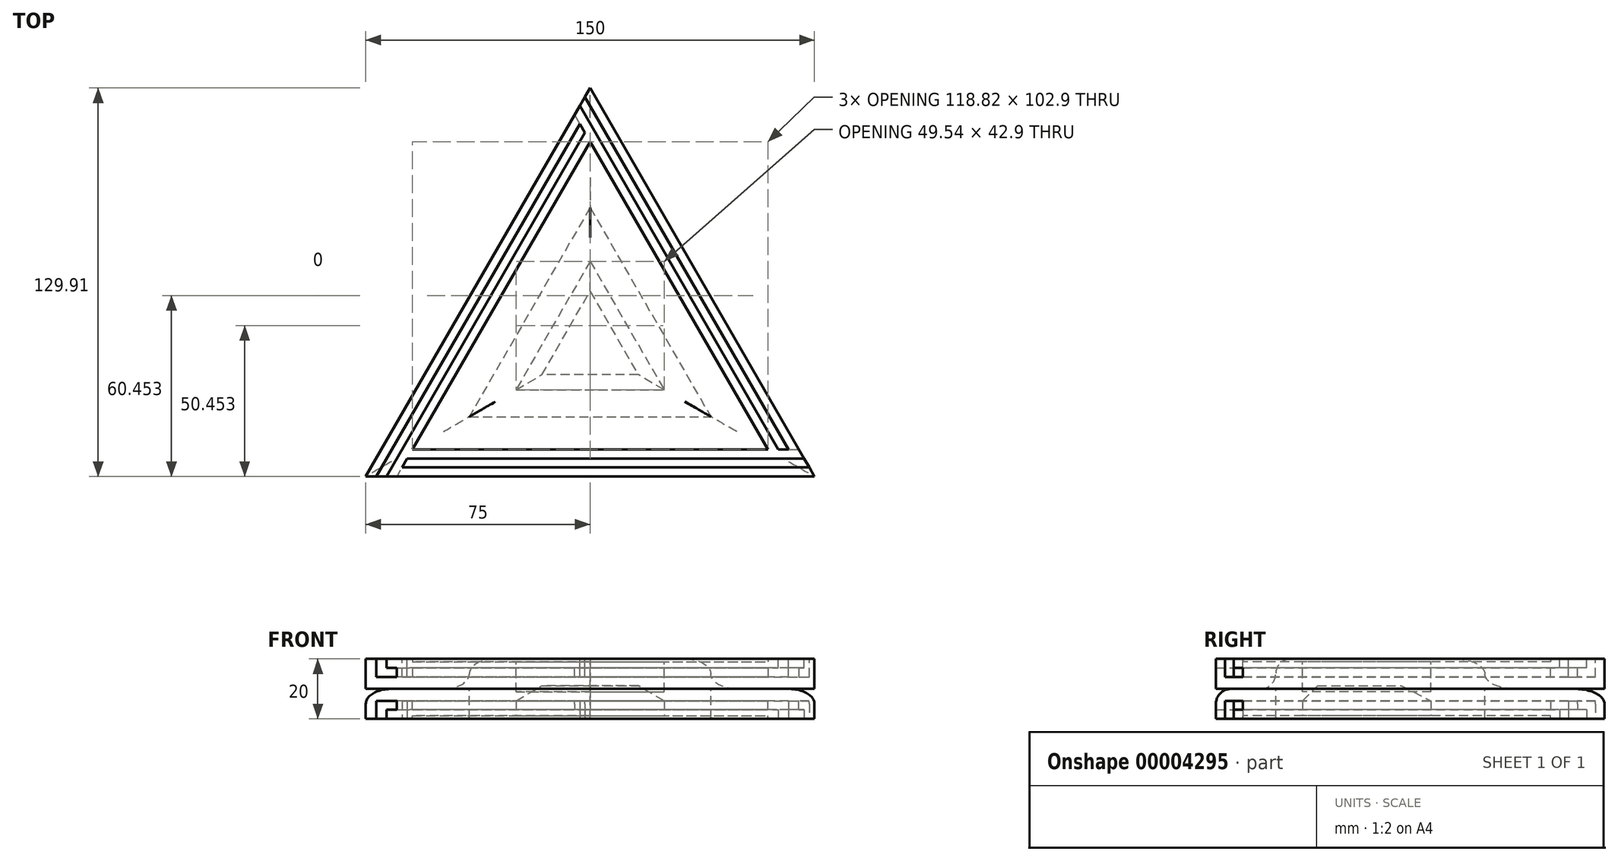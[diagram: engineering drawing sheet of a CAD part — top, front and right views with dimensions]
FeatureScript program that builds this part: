
annotation { "Feature Type Name" : "Feature", "Feature Type Description" : "" }
export const myFeature = defineFeature(function(context is Context, id is Id, definition is map)
    precondition{}
    {
        {
            var Q0;
            Q0=qCreatedBy(makeId("Top.planeOp"),FACE);
            var sketch = newSketch(context, id + "F0", { "sketchPlane" : qUnion([Q0])});
            skLineSegment(sketch, "E0.0", {"start": v(-75, -54.93) * mm, "end": v(75, -54.93) * mm});
            skLineSegment(sketch, "E1", {"start": v(0, 74.98) * mm, "end": v(-75, -54.93) * mm});
            skLineSegment(sketch, "E2", {"start": v(0, 74.98) * mm, "end": v(75, -54.93) * mm});
            skSolve(sketch);
        }
        {
            var Q0;
            Q0=makeQuery(id+"F0.imprint","IMPRINT",FACE,{"disambiguationData":[TD([[makeQuery(id+"F0.imprint","IMPRINT",EDGE,{"derivedFrom":sQuery(id+"F0.wireOp",EDGE,"E0.0")}),1.0]])]});
            extrude(context, id + "F1", {"entities" : qUnion([Q0]), "depth" : 10 * mm});
        }
        {
            var Q0;
            Q0=makeQuery(id+"F1.opExtrude","CAP_FACE",FACE,{"disambiguationData":[OSD([sQuery(id+"F0.wireOp",EDGE,"E0.0"),sQuery(id+"F0.wireOp",EDGE,"E1"),sQuery(id+"F0.wireOp",EDGE,"E2")])],"isStart":true});
            var sketch = newSketch(context, id + "F2", { "sketchPlane" : qUnion([Q0])});
            skLineSegment(sketch, "E3.0", {"start": v(-40.36, 34.93) * mm, "end": v(40.36, 34.93) * mm});
            skLineSegment(sketch, "E3.1", {"start": v(0, -34.98) * mm, "end": v(-40.36, 34.93) * mm});
            skLineSegment(sketch, "E3.2", {"start": v(0, -34.98) * mm, "end": v(40.36, 34.93) * mm});
            skSolve(sketch);
        }
        {
            var Q0;
            Q0=makeQuery(id+"F2.imprint","IMPRINT",FACE,{"disambiguationData":[TD([[makeQuery(id+"F2.imprint","IMPRINT",EDGE,{"derivedFrom":sQuery(id+"F2.wireOp",EDGE,"E3.0")}),-1.0]])]});
            extrude(context, id + "F3", {"entities" : qUnion([Q0]), "operationType" : NewBodyOperationType.ADD, "depth" : 10 * mm});
        }
        {
            var Q0;
            Q0=makeQuery(id+"F1.opExtrude","CAP_FACE",FACE,{"disambiguationData":[OSD([sQuery(id+"F0.wireOp",EDGE,"E0.0"),sQuery(id+"F0.wireOp",EDGE,"E1"),sQuery(id+"F0.wireOp",EDGE,"E2")])],"isStart":false});
            shell(context, id + "F4", {"entities" : qUnion([Q0]), "thickness" : 9 * mm});
        }
        {
            var Q0;
            Q0=makeQuery(id+"F1.opExtrude","CAP_FACE",FACE,{"disambiguationData":[OSD([sQuery(id+"F0.wireOp",EDGE,"E0.0"),sQuery(id+"F0.wireOp",EDGE,"E1"),sQuery(id+"F0.wireOp",EDGE,"E2")])],"isStart":false});
            var sketch = newSketch(context, id + "F5", { "sketchPlane" : qUnion([Q0])});
            skLineSegment(sketch, "E4", {"start": v(75, -54.93) * mm, "end": v(0, 74.98) * mm});
            skLineSegment(sketch, "E5", {"start": v(0, 74.98) * mm, "end": v(-75, -54.93) * mm});
            skLineSegment(sketch, "E6", {"start": v(-75, -54.93) * mm, "end": v(75, -54.93) * mm});
            skLineSegment(sketch, "E7.0", {"start": v(71.54, -54.93) * mm, "end": v(-1.73, 71.98) * mm});
            skLineSegment(sketch, "E8.0", {"start": v(1.73, 71.98) * mm, "end": v(-71.54, -54.93) * mm});
            skLineSegment(sketch, "E9.0", {"start": v(-73.27, -51.93) * mm, "end": v(73.27, -51.93) * mm});
            skLineSegment(sketch, "E10.0", {"start": v(-71.54, -48.93) * mm, "end": v(71.54, -48.93) * mm});
            skLineSegment(sketch, "E11.0", {"start": v(3.46, 68.98) * mm, "end": v(-68.07, -54.93) * mm});
            skLineSegment(sketch, "E12.0", {"start": v(68.07, -54.93) * mm, "end": v(-3.46, 68.98) * mm});
            skLineSegment(sketch, "E13", {"start": v(5.01, 66.3) * mm, "end": v(-64.58, -54.93) * mm});
            skLineSegment(sketch, "E14", {"start": v(-59.41, -45.93) * mm, "end": v(59.41, -45.93) * mm});
            skLineSegment(sketch, "E15", {"start": v(69.8, -45.93) * mm, "end": v(-69.8, -45.93) * mm});
            skLineSegment(sketch, "E16.0", {"start": v(64.6, -54.93) * mm, "end": v(-6.21, 67.74) * mm});
            skSolve(sketch);
        }
        {
            var Q0;
            {var subQ3=sQuery(id+"F5.wireOp",EDGE,"E4");var subQ5=sQuery(id+"F5.wireOp",EDGE,"E9.0");var subQ7=makeQuery(id+"F5.imprint","INTERSECT",VERTEX,{"derivedFrom":[subQ3,subQ5]});Q0=makeQuery(id+"F5.imprint","IMPRINT",FACE,{"disambiguationData":[TD([[makeQuery(id+"F5.imprint","IMPRINT",EDGE,{"disambiguationData":[TD([[subQ7,1.0]])],"derivedFrom":subQ3}),-1.0]])]});}
            var Q1;
            {var subQ3=sQuery(id+"F5.wireOp",EDGE,"E9.0");var subQ5=sQuery(id+"F5.wireOp",EDGE,"E7.0");var subQ7=makeQuery(id+"F5.imprint","INTERSECT",VERTEX,{"derivedFrom":[subQ5,subQ3]});Q1=makeQuery(id+"F5.imprint","IMPRINT",FACE,{"disambiguationData":[TD([[makeQuery(id+"F5.imprint","IMPRINT",EDGE,{"disambiguationData":[TD([[subQ7,-1.0]])],"derivedFrom":subQ5}),1.0]])]});}
            var Q2;
            {var subQ0=sQuery(id+"F5.wireOp",EDGE,"E16.0");var subQ3=sQuery(id+"F5.wireOp",EDGE,"E9.0");var subQ4=makeQuery(id+"F5.imprint","INTERSECT",VERTEX,{"derivedFrom":[subQ3,subQ0]});Q2=makeQuery(id+"F5.imprint","IMPRINT",FACE,{"disambiguationData":[TD([[makeQuery(id+"F5.imprint","IMPRINT",EDGE,{"disambiguationData":[TD([[subQ4,-1.0]])],"derivedFrom":subQ3}),1.0]])]});}
            var Q3;
            {var subQ3=sQuery(id+"F5.wireOp",EDGE,"E9.0");var subQ5=sQuery(id+"F5.wireOp",EDGE,"E13");var subQ7=makeQuery(id+"F5.imprint","INTERSECT",VERTEX,{"derivedFrom":[subQ3,subQ5]});Q3=makeQuery(id+"F5.imprint","IMPRINT",FACE,{"disambiguationData":[TD([[makeQuery(id+"F5.imprint","IMPRINT",EDGE,{"disambiguationData":[TD([[subQ7,-1.0]])],"derivedFrom":subQ3}),1.0]])]});}
            var Q4;
            {var subQ3=sQuery(id+"F5.wireOp",EDGE,"E6");var subQ5=sQuery(id+"F5.wireOp",EDGE,"E8.0");var subQ7=makeQuery(id+"F5.imprint","INTERSECT",VERTEX,{"derivedFrom":[subQ3,subQ5]});Q4=makeQuery(id+"F5.imprint","IMPRINT",FACE,{"disambiguationData":[TD([[makeQuery(id+"F5.imprint","IMPRINT",EDGE,{"disambiguationData":[TD([[subQ7,-1.0]])],"derivedFrom":subQ3}),1.0]])]});}
            var Q5;
            {var subQ1=sQuery(id+"F5.wireOp",EDGE,"E10.0");var subQ5=sQuery(id+"F5.wireOp",EDGE,"E8.0");var subQ6=makeQuery(id+"F5.imprint","INTERSECT",VERTEX,{"derivedFrom":[subQ5,subQ1]});Q5=makeQuery(id+"F5.imprint","IMPRINT",FACE,{"disambiguationData":[TD([[makeQuery(id+"F5.imprint","IMPRINT",EDGE,{"disambiguationData":[TD([[subQ6,-1.0]])],"derivedFrom":subQ5}),1.0]])]});}
            var Q6;
            {var subQ0=sQuery(id+"F5.wireOp",EDGE,"E16.0");var subQ3=sQuery(id+"F5.wireOp",EDGE,"E8.0");var subQ4=makeQuery(id+"F5.imprint","INTERSECT",VERTEX,{"derivedFrom":[subQ3,subQ0]});Q6=makeQuery(id+"F5.imprint","IMPRINT",FACE,{"disambiguationData":[TD([[makeQuery(id+"F5.imprint","IMPRINT",EDGE,{"disambiguationData":[TD([[subQ4,-1.0]])],"derivedFrom":subQ3}),1.0]])]});}
            var Q7;
            {var subQ0=sQuery(id+"F5.wireOp",EDGE,"E15");var subQ3=sQuery(id+"F5.wireOp",EDGE,"E8.0");var subQ4=makeQuery(id+"F5.imprint","INTERSECT",VERTEX,{"derivedFrom":[subQ3,subQ0]});Q7=makeQuery(id+"F5.imprint","IMPRINT",FACE,{"disambiguationData":[TD([[makeQuery(id+"F5.imprint","IMPRINT",EDGE,{"disambiguationData":[TD([[subQ4,-1.0]])],"derivedFrom":subQ3}),1.0]])]});}
            var Q8;
            {var subQ3=sQuery(id+"F5.wireOp",EDGE,"E5");var subQ5=sQuery(id+"F5.wireOp",EDGE,"E7.0");var subQ7=makeQuery(id+"F5.imprint","INTERSECT",VERTEX,{"derivedFrom":[subQ3,subQ5]});Q8=makeQuery(id+"F5.imprint","IMPRINT",FACE,{"disambiguationData":[TD([[makeQuery(id+"F5.imprint","IMPRINT",EDGE,{"disambiguationData":[TD([[subQ7,-1.0]])],"derivedFrom":subQ3}),1.0]])]});}
            var Q9;
            {var subQ1=sQuery(id+"F5.wireOp",EDGE,"E11.0");var subQ5=sQuery(id+"F5.wireOp",EDGE,"E7.0");var subQ6=makeQuery(id+"F5.imprint","INTERSECT",VERTEX,{"derivedFrom":[subQ5,subQ1]});Q9=makeQuery(id+"F5.imprint","IMPRINT",FACE,{"disambiguationData":[TD([[makeQuery(id+"F5.imprint","IMPRINT",EDGE,{"disambiguationData":[TD([[subQ6,-1.0]])],"derivedFrom":subQ5}),1.0]])]});}
            var Q10;
            {var subQ0=sQuery(id+"F5.wireOp",EDGE,"E13");var subQ3=sQuery(id+"F5.wireOp",EDGE,"E7.0");var subQ4=makeQuery(id+"F5.imprint","INTERSECT",VERTEX,{"derivedFrom":[subQ3,subQ0]});Q10=makeQuery(id+"F5.imprint","IMPRINT",FACE,{"disambiguationData":[TD([[makeQuery(id+"F5.imprint","IMPRINT",EDGE,{"disambiguationData":[TD([[subQ4,-1.0]])],"derivedFrom":subQ3}),1.0]])]});}
            var Q11;
            {var subQ0=sQuery(id+"F5.wireOp",EDGE,"E15");var subQ3=sQuery(id+"F5.wireOp",EDGE,"E7.0");var subQ4=makeQuery(id+"F5.imprint","INTERSECT",VERTEX,{"derivedFrom":[subQ3,subQ0]});Q11=makeQuery(id+"F5.imprint","IMPRINT",FACE,{"disambiguationData":[TD([[makeQuery(id+"F5.imprint","IMPRINT",EDGE,{"disambiguationData":[TD([[subQ4,-1.0]])],"derivedFrom":subQ3}),1.0]])]});}
            extrude(context, id + "F6", {"entities" : qUnion([Q0, Q1, Q2, Q3, Q4, Q5, Q6, Q7, Q8, Q9, Q10, Q11]), "operationType" : NewBodyOperationType.REMOVE, "oppositeDirection" : true, "depth" : 6 * mm});
        }
        {
            var Q0;
            Q0=makeQuery(id+"F6.boolean.opBoolean","COPY",FACE,{"derivedFrom":makeQuery(id+"F6.opExtrude","SWEPT_FACE",FACE,{"disambiguationData":[OSD([sQuery(id+"F5.wireOp",EDGE,"E12.0")])]})});
            var sketch = newSketch(context, id + "F7", { "sketchPlane" : qUnion([Q0])});
            skLineSegment(sketch, "E17", {"start": v(61.47, 4) * mm, "end": v(-71.21, 4) * mm});
            skLineSegment(sketch, "E18.0", {"start": v(61.47, 7) * mm, "end": v(-71.21, 7) * mm});
            skSolve(sketch);
        }
        {
            var Q0;
            {var subQ3=sQuery(id+"F7.wireOp",EDGE,"E17");Q0=makeQuery(id+"F7.imprint","IMPRINT",FACE,{"disambiguationData":[TD([[makeQuery(id+"F7.imprint","IMPRINT",EDGE,{"derivedFrom":subQ3}),1.0]])]});}
            extrude(context, id + "F8", {"entities" : qUnion([Q0]), "operationType" : NewBodyOperationType.REMOVE, "oppositeDirection" : true, "depth" : 3 * mm});
        }
        {
            var Q0;
            Q0=makeQuery(id+"F6.boolean.opBoolean","COPY",FACE,{"derivedFrom":makeQuery(id+"F6.opExtrude","SWEPT_FACE",FACE,{"disambiguationData":[OSD([sQuery(id+"F5.wireOp",EDGE,"E10.0")])]})});
            var sketch = newSketch(context, id + "F9", { "sketchPlane" : qUnion([Q0])});
            skLineSegment(sketch, "E19", {"start": v(71.54, 4) * mm, "end": v(-61.13, 4) * mm});
            skLineSegment(sketch, "E20.0", {"start": v(71.54, 7) * mm, "end": v(-61.13, 7) * mm});
            skSolve(sketch);
        }
        {
            var Q0;
            {var subQ3=sQuery(id+"F9.wireOp",EDGE,"E19");Q0=makeQuery(id+"F9.imprint","IMPRINT",FACE,{"disambiguationData":[TD([[makeQuery(id+"F9.imprint","IMPRINT",EDGE,{"derivedFrom":subQ3}),1.0]])]});}
            extrude(context, id + "F10", {"entities" : qUnion([Q0]), "operationType" : NewBodyOperationType.REMOVE, "oppositeDirection" : true, "depth" : 3 * mm});
        }
        {
            var Q0;
            Q0=makeQuery(id+"F6.boolean.opBoolean","COPY",FACE,{"derivedFrom":makeQuery(id+"F6.opExtrude","SWEPT_FACE",FACE,{"disambiguationData":[OSD([sQuery(id+"F5.wireOp",EDGE,"E11.0")])]})});
            var sketch = newSketch(context, id + "F11", { "sketchPlane" : qUnion([Q0])});
            skLineSegment(sketch, "E21", {"start": v(81.6, 4) * mm, "end": v(-51.07, 4) * mm});
            skLineSegment(sketch, "E22.0", {"start": v(81.6, 7) * mm, "end": v(-51.07, 7) * mm});
            skSolve(sketch);
        }
        {
            var Q0;
            {var subQ4=sQuery(id+"F11.wireOp",EDGE,"E21");Q0=makeQuery(id+"F11.imprint","IMPRINT",FACE,{"disambiguationData":[TD([[makeQuery(id+"F11.imprint","IMPRINT",EDGE,{"derivedFrom":subQ4}),1.0]])]});}
            extrude(context, id + "F12", {"entities" : qUnion([Q0]), "operationType" : NewBodyOperationType.REMOVE, "oppositeDirection" : true, "depth" : 3 * mm});
        }
        {
            var Q0;
            Q0=makeQuery(id+"F1.opExtrude","SWEPT_BODY",BODY,{"disambiguationData":[OSD([sQuery(id+"F0.wireOp",EDGE,"E0.0"),sQuery(id+"F0.wireOp",EDGE,"E1"),sQuery(id+"F0.wireOp",EDGE,"E2")])]});
            var Q1;
            Q1=qCreatedBy(makeId("Top.planeOp"),FACE);
            mirror(context, id + "F13", {"entities" : qUnion([Q0]), "mirrorPlane" : qUnion([Q1])});
        }
        {
            var Q0;
            Q0=makeQuery(id+"F13.opPattern","COPY",FACE,{"derivedFrom":makeQuery(id+"F1.opExtrude","CAP_FACE",FACE,{"disambiguationData":[OSD([sQuery(id+"F0.wireOp",EDGE,"E0.0"),sQuery(id+"F0.wireOp",EDGE,"E1"),sQuery(id+"F0.wireOp",EDGE,"E2")])],"isStart":true}),"instanceName":"1"});
            fillet(context, id + "F14", {"entities" : qUnion([Q0]), "radius" : 5 * mm, "tangentPropagation" : true, "allowEdgeOverflow" : false});
        }
        {
            var Q0;
            Q0=makeQuery(id+"F13.opPattern","COPY",FACE,{"derivedFrom":makeQuery(id+"F3.opExtrude","CAP_FACE",FACE,{"disambiguationData":[OSD([sQuery(id+"F2.wireOp",EDGE,"E3.0"),sQuery(id+"F2.wireOp",EDGE,"E3.1"),sQuery(id+"F2.wireOp",EDGE,"E3.2")])],"isStart":false}),"instanceName":"1"});
            fillet(context, id + "F15", {"entities" : qUnion([Q0]), "radius" : 5 * mm, "tangentPropagation" : true, "allowEdgeOverflow" : false});
        }
        {
            var Q0;
            {var subQ0=sQuery(id+"F2.wireOp",EDGE,"E3.0");Q0=makeQuery(id+"F13.opPattern","COPY",EDGE,{"derivedFrom":makeQuery(id+"F4.opShell","OFFSET_EDGE",EDGE,{"disambiguationData":[OSD([subQ0]),TDD([makeQuery(id+"F3.opExtrude","CAP_EDGE",EDGE,{"disambiguationData":[OSD([subQ0])],"isStart":true})])]}),"instanceName":"1"});}
            var Q1;
            {var subQ0=sQuery(id+"F2.wireOp",EDGE,"E3.2");Q1=makeQuery(id+"F13.opPattern","COPY",EDGE,{"derivedFrom":makeQuery(id+"F4.opShell","OFFSET_EDGE",EDGE,{"disambiguationData":[OSD([subQ0]),TDD([makeQuery(id+"F3.opExtrude","CAP_EDGE",EDGE,{"disambiguationData":[OSD([subQ0])],"isStart":true})])]}),"instanceName":"1"});}
            var Q2;
            {var subQ0=sQuery(id+"F2.wireOp",EDGE,"E3.1");Q2=makeQuery(id+"F13.opPattern","COPY",EDGE,{"derivedFrom":makeQuery(id+"F4.opShell","OFFSET_EDGE",EDGE,{"disambiguationData":[OSD([subQ0]),TDD([makeQuery(id+"F3.opExtrude","CAP_EDGE",EDGE,{"disambiguationData":[OSD([subQ0])],"isStart":true})])]}),"instanceName":"1"});}
            chamfer(context, id + "F16", {"entities" : qUnion([Q0, Q1, Q2]), "width" : 5 * mm, "tangentPropagation" : true});
        }
    });
